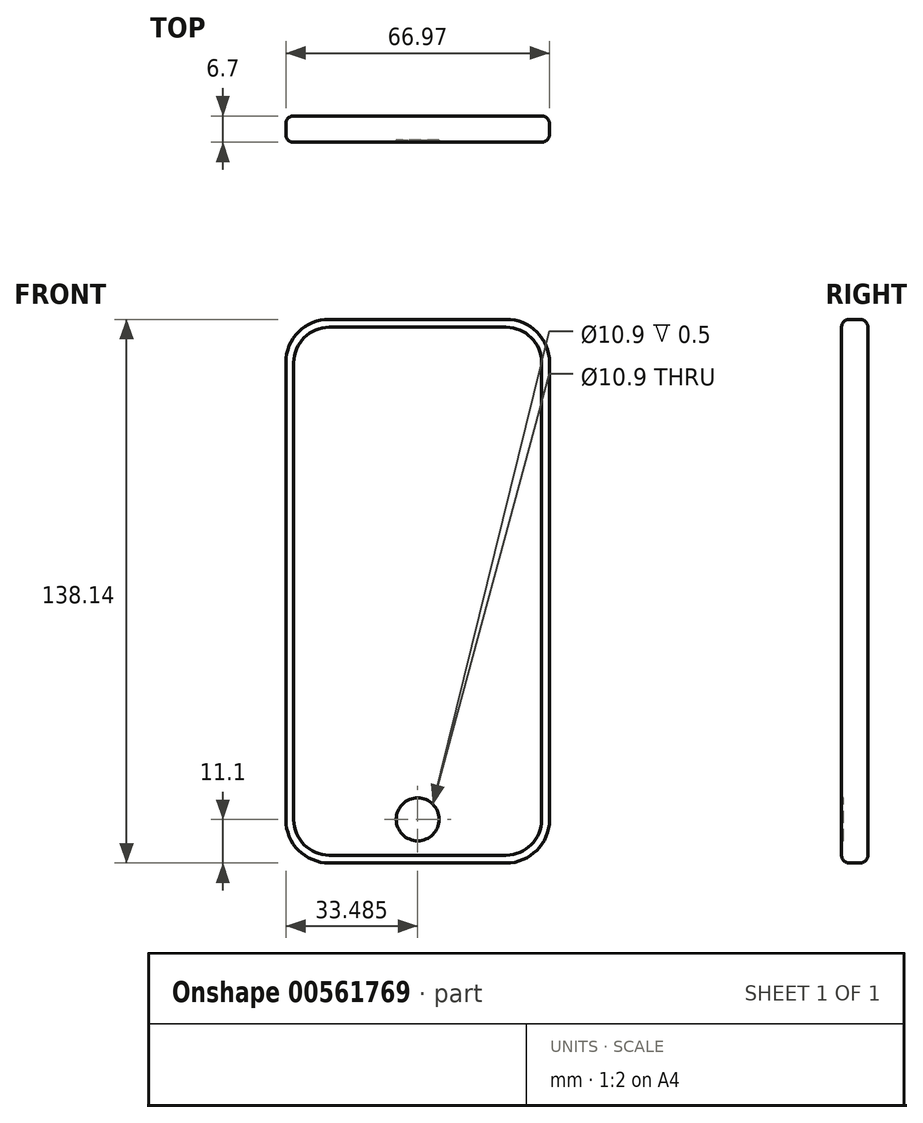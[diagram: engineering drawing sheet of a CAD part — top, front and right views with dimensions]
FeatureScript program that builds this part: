
annotation { "Feature Type Name" : "Feature", "Feature Type Description" : "" }
export const myFeature = defineFeature(function(context is Context, id is Id, definition is map)
    precondition{}
    {
        {
            var Q0;
            Q0=qCreatedBy(makeId("Front.planeOp"),FACE);
            var sketch = newSketch(context, id + "F0", { "sketchPlane" : qUnion([Q0])});
            skLineSegment(sketch, "E0", {"start": v(0, 0) * mm, "end": v(0, 138.14) * mm});
            skLineSegment(sketch, "E1", {"start": v(0, 0) * mm, "end": v(66.97, 0) * mm});
            skLineSegment(sketch, "E2", {"start": v(0, 138.14) * mm, "end": v(66.97, 138.14) * mm});
            skLineSegment(sketch, "E3", {"start": v(66.97, 138.14) * mm, "end": v(66.97, 0) * mm});
            skSolve(sketch);
        }
        {
            var Q0;
            Q0=makeQuery(id+"F0.imprint","IMPRINT",FACE,{"disambiguationData":[TD([[makeQuery(id+"F0.imprint","IMPRINT",EDGE,{"derivedFrom":sQuery(id+"F0.wireOp",EDGE,"E0")}),-1.0]])]});
            extrude(context, id + "F1", {"entities" : qUnion([Q0]), "depth" : 6.7 * mm, "offsetDistance" : 25.4 * mm});
        }
        {
            var Q0;
            Q0=makeQuery(id+"F1.opExtrude","SWEPT_EDGE",EDGE,{"disambiguationData":[OSD([sQuery(id+"F0.wireOp",EDGE,"E0"),sQuery(id+"F0.wireOp",EDGE,"E2")])]});
            var Q1;
            Q1=makeQuery(id+"F1.opExtrude","SWEPT_EDGE",EDGE,{"disambiguationData":[OSD([sQuery(id+"F0.wireOp",EDGE,"E2"),sQuery(id+"F0.wireOp",EDGE,"E3")])]});
            var Q2;
            Q2=makeQuery(id+"F1.opExtrude","SWEPT_EDGE",EDGE,{"disambiguationData":[OSD([sQuery(id+"F0.wireOp",EDGE,"E1"),sQuery(id+"F0.wireOp",EDGE,"E3")])]});
            var Q3;
            Q3=makeQuery(id+"F1.opExtrude","SWEPT_EDGE",EDGE,{"disambiguationData":[OSD([sQuery(id+"F0.wireOp",EDGE,"E0"),sQuery(id+"F0.wireOp",EDGE,"E1")])]});
            fillet(context, id + "F2", {"entities" : qUnion([Q0, Q1, Q2, Q3]), "radius" : 11 * mm, "tangentPropagation" : true, "allowEdgeOverflow" : false});
        }
        {
            var Q0;
            Q0=makeQuery(id+"F1.opExtrude","CAP_FACE",FACE,{"disambiguationData":[OSD([sQuery(id+"F0.wireOp",EDGE,"E0"),sQuery(id+"F0.wireOp",EDGE,"E1"),sQuery(id+"F0.wireOp",EDGE,"E2"),sQuery(id+"F0.wireOp",EDGE,"E3")])],"isStart":false});
            fillet(context, id + "F3", {"entities" : qUnion([Q0]), "radius" : 2 * mm, "tangentPropagation" : true, "allowEdgeOverflow" : false});
        }
        {
            var Q0;
            Q0=makeQuery(id+"F1.opExtrude","CAP_FACE",FACE,{"disambiguationData":[OSD([sQuery(id+"F0.wireOp",EDGE,"E0"),sQuery(id+"F0.wireOp",EDGE,"E1"),sQuery(id+"F0.wireOp",EDGE,"E2"),sQuery(id+"F0.wireOp",EDGE,"E3")])],"isStart":true});
            fillet(context, id + "F4", {"entities" : qUnion([Q0]), "radius" : 2 * mm, "tangentPropagation" : true, "allowEdgeOverflow" : false});
        }
        {
            var Q0;
            Q0=makeQuery(id+"F1.opExtrude","CAP_FACE",FACE,{"disambiguationData":[OSD([sQuery(id+"F0.wireOp",EDGE,"E0"),sQuery(id+"F0.wireOp",EDGE,"E1"),sQuery(id+"F0.wireOp",EDGE,"E2"),sQuery(id+"F0.wireOp",EDGE,"E3")])],"isStart":false});
            var sketch = newSketch(context, id + "F5", { "sketchPlane" : qUnion([Q0])});
            skCircle(sketch, "E4", {"center": v(33.48, 11.1) * mm, "radius": 5.45 * mm});
            skSolve(sketch);
        }
        {
            var Q0;
            Q0=makeQuery(id+"F5.imprint","IMPRINT",FACE,{"disambiguationData":[TD([[makeQuery(id+"F5.imprint","IMPRINT",EDGE,{"derivedFrom":sQuery(id+"F5.wireOp",EDGE,"E4")}),1.0]])]});
            extrude(context, id + "F6", {"entities" : qUnion([Q0]), "oppositeDirection" : true, "depth" : 0.5 * mm, "offsetDistance" : 25.4 * mm});
        }
        {
            var Q0;
            Q0=makeQuery(id+"F6.opExtrude","SWEPT_BODY",BODY,{"disambiguationData":[OSD([sQuery(id+"F5.wireOp",EDGE,"E4")])]});
            var Q1;
            Q1=makeQuery(id+"F1.opExtrude","SWEPT_BODY",BODY,{"disambiguationData":[OSD([sQuery(id+"F0.wireOp",EDGE,"E0"),sQuery(id+"F0.wireOp",EDGE,"E1"),sQuery(id+"F0.wireOp",EDGE,"E2"),sQuery(id+"F0.wireOp",EDGE,"E3")])]});
            booleanBodies(context, id + "F7", {"operationType" : BooleanOperationType.SUBTRACTION, "tools" : qUnion([Q0]), "targets" : qUnion([Q1])});
        }
        {
            var Q0;
            Q0=makeQuery(id+"F5.imprint","IMPRINT",FACE,{"disambiguationData":[TD([[makeQuery(id+"F5.imprint","IMPRINT",EDGE,{"derivedFrom":sQuery(id+"F5.wireOp",EDGE,"E4")}),-1.0]])]});
            extrude(context, id + "F8", {"entities" : qUnion([Q0]), "depth" : 0 * mm, "offsetDistance" : 25.4 * mm});
        }
        {
            var Q0;
            Q0=makeQuery(id+"F5.imprint","IMPRINT",FACE,{"disambiguationData":[TD([[makeQuery(id+"F5.imprint","IMPRINT",EDGE,{"derivedFrom":sQuery(id+"F5.wireOp",EDGE,"E4")}),1.0]])]});
            extrude(context, id + "F9", {"entities" : qUnion([Q0]), "depth" : 0 * mm, "offsetDistance" : 25.4 * mm});
        }
        {
            var Q0;
            Q0=makeQuery(id+"F9.opExtrude","SWEPT_BODY",BODY,{"disambiguationData":[OSD([sQuery(id+"F5.wireOp",EDGE,"E4")])]});
            deleteBodies(context, id + "F10", {"entities" : qUnion([Q0])});
        }
        {
            var Q0;
            Q0=makeQuery(id+"F5.imprint","IMPRINT",FACE,{"disambiguationData":[TD([[makeQuery(id+"F5.imprint","IMPRINT",EDGE,{"derivedFrom":sQuery(id+"F5.wireOp",EDGE,"E4")}),1.0]])]});
            extrude(context, id + "F11", {"entities" : qUnion([Q0]), "oppositeDirection" : true, "depth" : 0 * mm, "offsetDistance" : 25.4 * mm});
        }
        {
            var Q0;
            Q0=makeQuery(id+"F11.opExtrude","SWEPT_BODY",BODY,{"disambiguationData":[OSD([sQuery(id+"F5.wireOp",EDGE,"E4")])]});
            deleteBodies(context, id + "F12", {"entities" : qUnion([Q0])});
        }
    });
